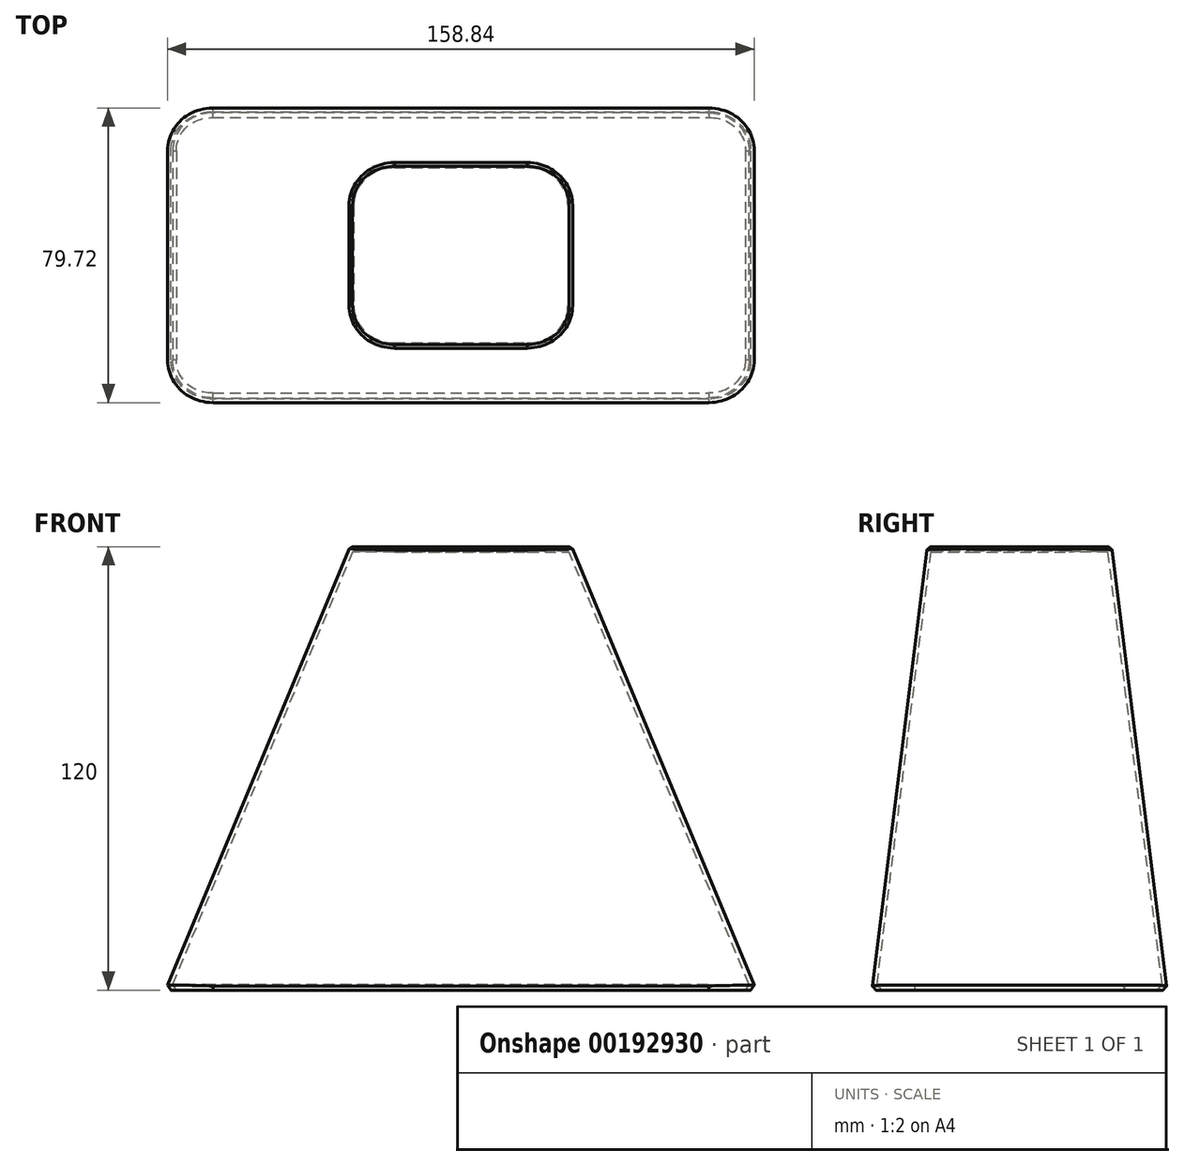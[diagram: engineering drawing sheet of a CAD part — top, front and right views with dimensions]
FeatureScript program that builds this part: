
annotation { "Feature Type Name" : "Feature", "Feature Type Description" : "" }
export const myFeature = defineFeature(function(context is Context, id is Id, definition is map)
    precondition{}
    {
        {
            var Q0;
            Q0=qCreatedBy(makeId("Top.planeOp"),FACE);
            var sketch = newSketch(context, id + "F0", { "sketchPlane" : qUnion([Q0])});
            skLineSegment(sketch, "E0.bottom", {"start": v(80, -40) * mm, "end": v(-80, -40) * mm});
            skLineSegment(sketch, "E0.top", {"start": v(80, 40) * mm, "end": v(-80, 40) * mm});
            skLineSegment(sketch, "E0.left", {"start": v(80, -40) * mm, "end": v(80, 40) * mm});
            skLineSegment(sketch, "E0.right", {"start": v(-80, -40) * mm, "end": v(-80, 40) * mm});
            skPoint(sketch, "E0.middle", {"position": v(0, 0) * mm});
            skSolve(sketch);
        }
        {
            var Q0;
            Q0 = qSketchRegion(id + "F0", true);
            extrude(context, id + "F1", {"entities" : qUnion([Q0]), "depth" : 120 * mm});
        }
        {
            var Q0;
            Q0=makeQuery(id+"F1.opExtrude","CAP_EDGE",EDGE,{"disambiguationData":[OSD([sQuery(id+"F0.wireOp",EDGE,"E0.right")])],"isStart":false});
            var Q1;
            Q1=makeQuery(id+"F1.opExtrude","CAP_EDGE",EDGE,{"disambiguationData":[OSD([sQuery(id+"F0.wireOp",EDGE,"E0.left")])],"isStart":false});
            chamfer(context, id + "F2", {"entities" : qUnion([Q0, Q1]), "chamferType" : ChamferType.TWO_OFFSETS, "width1" : 120 * mm, "oppositeDirection" : false, "width2" : 50 * mm, "tangentPropagation" : true});
        }
        {
            var Q0;
            Q0=makeQuery(id+"F1.opExtrude","CAP_EDGE",EDGE,{"disambiguationData":[OSD([sQuery(id+"F0.wireOp",EDGE,"E0.bottom")])],"isStart":false});
            var Q1;
            Q1=makeQuery(id+"F1.opExtrude","CAP_EDGE",EDGE,{"disambiguationData":[OSD([sQuery(id+"F0.wireOp",EDGE,"E0.top")])],"isStart":false});
            chamfer(context, id + "F3", {"entities" : qUnion([Q0, Q1]), "chamferType" : ChamferType.TWO_OFFSETS, "width1" : 15 * mm, "oppositeDirection" : true, "width2" : 120 * mm, "tangentPropagation" : true});
        }
        {
            var Q0;
            Q0=makeQuery(id+"F3.opChamfer","BLEND_EDGE",EDGE,{"blendedFrom":[makeQuery(id+"F1.opExtrude","CAP_EDGE",EDGE,{"disambiguationData":[OSD([sQuery(id+"F0.wireOp",EDGE,"E0.top")])],"isStart":false}),makeQuery(id+"F2.opChamfer","BLEND_FACE",FACE,{"disambiguationData":[OSD([sQuery(id+"F0.wireOp",EDGE,"E0.right")])]})],"blendedInto":[makeQuery(id+"F2.opChamfer","BLEND_FACE",FACE,{"disambiguationData":[OSD([sQuery(id+"F0.wireOp",EDGE,"E0.right")])]})]});
            var Q1;
            Q1=makeQuery(id+"F3.opChamfer","BLEND_EDGE",EDGE,{"blendedFrom":[makeQuery(id+"F1.opExtrude","CAP_EDGE",EDGE,{"disambiguationData":[OSD([sQuery(id+"F0.wireOp",EDGE,"E0.bottom")])],"isStart":false}),makeQuery(id+"F2.opChamfer","BLEND_FACE",FACE,{"disambiguationData":[OSD([sQuery(id+"F0.wireOp",EDGE,"E0.right")])]})],"blendedInto":[makeQuery(id+"F2.opChamfer","BLEND_FACE",FACE,{"disambiguationData":[OSD([sQuery(id+"F0.wireOp",EDGE,"E0.right")])]})]});
            var Q2;
            Q2=makeQuery(id+"F3.opChamfer","BLEND_EDGE",EDGE,{"blendedFrom":[makeQuery(id+"F1.opExtrude","CAP_EDGE",EDGE,{"disambiguationData":[OSD([sQuery(id+"F0.wireOp",EDGE,"E0.bottom")])],"isStart":false}),makeQuery(id+"F2.opChamfer","BLEND_FACE",FACE,{"disambiguationData":[OSD([sQuery(id+"F0.wireOp",EDGE,"E0.left")])]})],"blendedInto":[makeQuery(id+"F2.opChamfer","BLEND_FACE",FACE,{"disambiguationData":[OSD([sQuery(id+"F0.wireOp",EDGE,"E0.left")])]})]});
            var Q3;
            Q3=makeQuery(id+"F3.opChamfer","BLEND_EDGE",EDGE,{"blendedFrom":[makeQuery(id+"F1.opExtrude","CAP_EDGE",EDGE,{"disambiguationData":[OSD([sQuery(id+"F0.wireOp",EDGE,"E0.top")])],"isStart":false}),makeQuery(id+"F2.opChamfer","BLEND_FACE",FACE,{"disambiguationData":[OSD([sQuery(id+"F0.wireOp",EDGE,"E0.left")])]})],"blendedInto":[makeQuery(id+"F2.opChamfer","BLEND_FACE",FACE,{"disambiguationData":[OSD([sQuery(id+"F0.wireOp",EDGE,"E0.left")])]})]});
            fillet(context, id + "F4", {"entities" : qUnion([Q0, Q1, Q2, Q3]), "radius" : 12 * mm, "tangentPropagation" : true, "allowEdgeOverflow" : false});
        }
        {
            var Q0;
            {var subQ0=sQuery(id+"F0.wireOp",EDGE,"E0.bottom");Q0=makeQuery(id+"F3.opChamfer","BLEND_EDGE",EDGE,{"blendedFrom":[makeQuery(id+"F1.opExtrude","CAP_EDGE",EDGE,{"disambiguationData":[OSD([subQ0])],"isStart":false}),makeQuery(id+"F1.opExtrude","CAP_FACE",FACE,{"disambiguationData":[OSD([subQ0,sQuery(id+"F0.wireOp",EDGE,"E0.top"),sQuery(id+"F0.wireOp",EDGE,"E0.left"),sQuery(id+"F0.wireOp",EDGE,"E0.right")])],"isStart":false})],"blendedInto":[makeQuery(id+"F1.opExtrude","CAP_FACE",FACE,{"disambiguationData":[OSD([subQ0,sQuery(id+"F0.wireOp",EDGE,"E0.top"),sQuery(id+"F0.wireOp",EDGE,"E0.left"),sQuery(id+"F0.wireOp",EDGE,"E0.right")])],"isStart":false})]});}
            chamfer(context, id + "F5", {"entities" : qUnion([Q0]), "width" : 1 * mm, "tangentPropagation" : true});
        }
        {
            var Q0;
            {var subQ0=sQuery(id+"F0.wireOp",EDGE,"E0.right");Q0=makeQuery(id+"F2.opChamfer","BLEND_EDGE",EDGE,{"blendedFrom":[makeQuery(id+"F1.opExtrude","CAP_EDGE",EDGE,{"disambiguationData":[OSD([subQ0])],"isStart":false}),makeQuery(id+"F1.opExtrude","CAP_FACE",FACE,{"disambiguationData":[OSD([sQuery(id+"F0.wireOp",EDGE,"E0.bottom"),sQuery(id+"F0.wireOp",EDGE,"E0.top"),sQuery(id+"F0.wireOp",EDGE,"E0.left"),subQ0])],"isStart":true})],"blendedInto":[makeQuery(id+"F1.opExtrude","CAP_FACE",FACE,{"disambiguationData":[OSD([sQuery(id+"F0.wireOp",EDGE,"E0.bottom"),sQuery(id+"F0.wireOp",EDGE,"E0.top"),sQuery(id+"F0.wireOp",EDGE,"E0.left"),subQ0])],"isStart":true})]});}
            chamfer(context, id + "F6", {"entities" : qUnion([Q0]), "width" : 1 * mm, "tangentPropagation" : true});
        }
        {
            var Q0;
            Q0=makeQuery(id+"F1.opExtrude","CAP_FACE",FACE,{"disambiguationData":[OSD([sQuery(id+"F0.wireOp",EDGE,"E0.bottom"),sQuery(id+"F0.wireOp",EDGE,"E0.top"),sQuery(id+"F0.wireOp",EDGE,"E0.left"),sQuery(id+"F0.wireOp",EDGE,"E0.right")])],"isStart":true});
            shell(context, id + "F7", {"entities" : qUnion([Q0]), "thickness" : 1.2 * mm});
        }
    });
